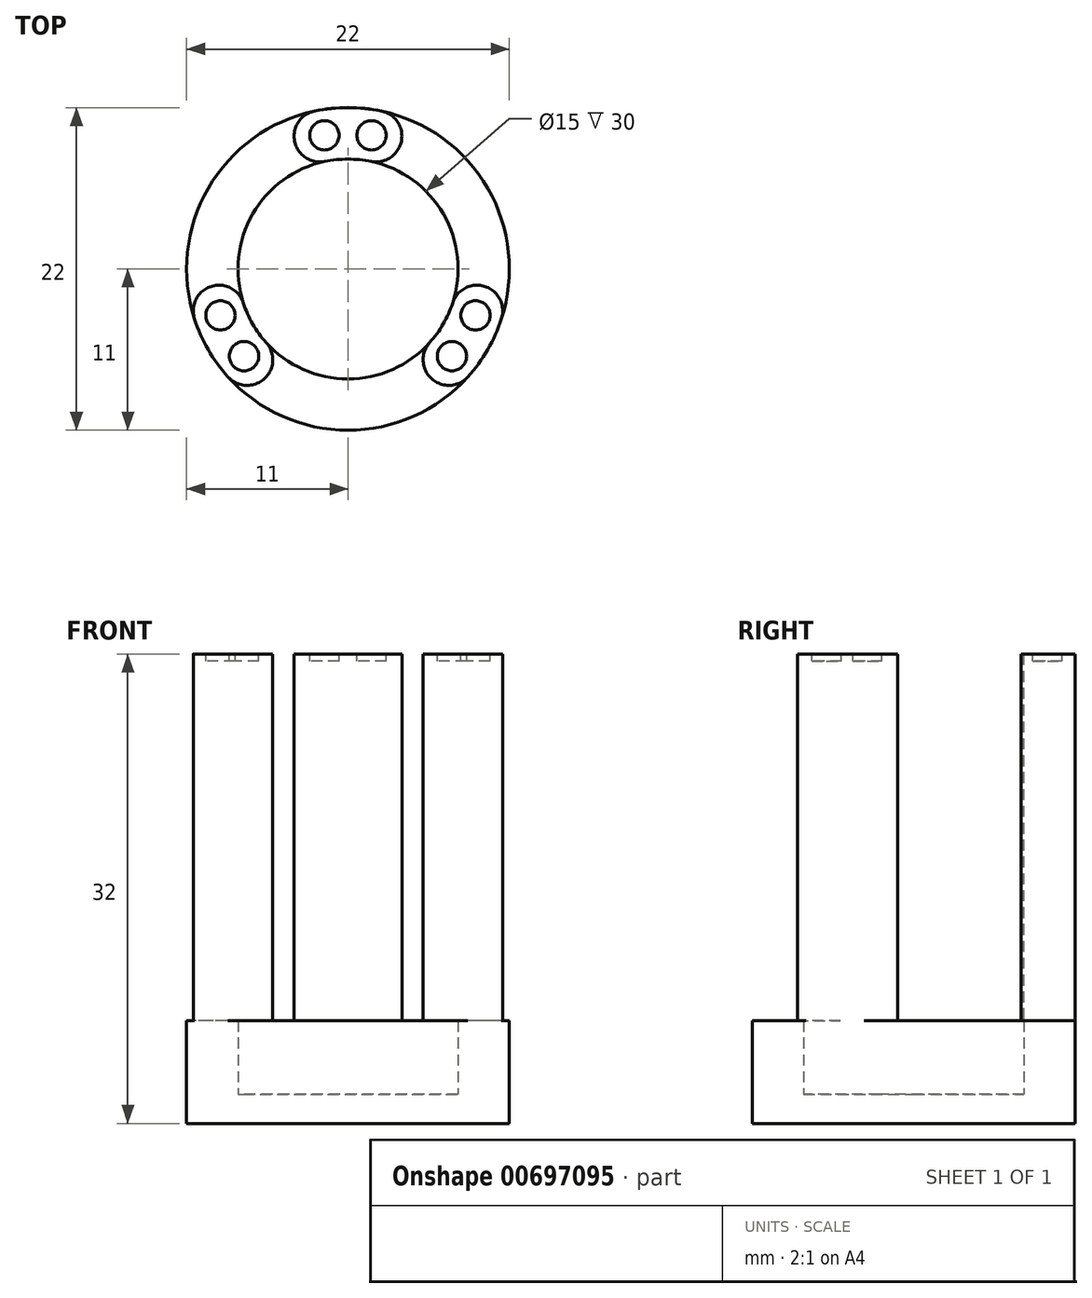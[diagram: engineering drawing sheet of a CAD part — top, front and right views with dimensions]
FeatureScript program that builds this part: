
annotation { "Feature Type Name" : "Feature", "Feature Type Description" : "" }
export const myFeature = defineFeature(function(context is Context, id is Id, definition is map)
    precondition{}
    {
        {
            var Q0;
            Q0=qCreatedBy(makeId("Top.planeOp"),FACE);
            var sketch = newSketch(context, id + "F0", { "sketchPlane" : qUnion([Q0])});
            skCircle(sketch, "E0", {"center": v(0, 0) * mm, "radius": 11 * mm});
            skSolve(sketch);
        }
        {
            var Q0;
            Q0=makeQuery(id+"F0.imprint","IMPRINT",FACE,{"disambiguationData":[TD([[makeQuery(id+"F0.imprint","IMPRINT",EDGE,{"derivedFrom":sQuery(id+"F0.wireOp",EDGE,"E0")}),1.0]])]});
            extrude(context, id + "F1", {"entities" : qUnion([Q0]), "depth" : 2 * mm, "offsetDistance" : 25 * mm});
        }
        {
            var Q0;
            Q0=makeQuery(id+"F1.opExtrude","CAP_FACE",FACE,{"disambiguationData":[OSD([sQuery(id+"F0.wireOp",EDGE,"E0")])],"isStart":false});
            var sketch = newSketch(context, id + "F2", { "sketchPlane" : qUnion([Q0])});
            skCircle(sketch, "E1", {"center": v(0, 0) * mm, "radius": 11 * mm});
            skCircle(sketch, "E2", {"center": v(0, 0) * mm, "radius": 7.5 * mm});
            skSolve(sketch);
        }
        {
            var Q0;
            Q0=makeQuery(id+"F2.imprint","IMPRINT",FACE,{"disambiguationData":[TD([[makeQuery(id+"F2.imprint","IMPRINT",EDGE,{"derivedFrom":sQuery(id+"F2.wireOp",EDGE,"E1")}),1.0]])]});
            extrude(context, id + "F3", {"entities" : qUnion([Q0]), "operationType" : NewBodyOperationType.ADD, "depth" : 5 * mm, "offsetDistance" : 25 * mm});
        }
        {
            var Q0;
            Q0=makeQuery(id+"F3.opExtrude","CAP_FACE",FACE,{"disambiguationData":[OSD([sQuery(id+"F2.wireOp",EDGE,"E1"),sQuery(id+"F2.wireOp",EDGE,"E2")])],"isStart":false});
            var sketch = newSketch(context, id + "F4", { "sketchPlane" : qUnion([Q0])});
            skCircle(sketch, "E3", {"center": v(0, 0) * mm, "radius": 9.25 * mm, "construction": true});
            skLineSegment(sketch, "E4", {"start": v(0, 0) * mm, "end": v(0, 9.25) * mm, "construction": true});
            skLineSegment(sketch, "E5", {"start": v(0, 0) * mm, "end": v(8.01, -4.62) * mm, "construction": true});
            skLineSegment(sketch, "E6", {"start": v(0, 0) * mm, "end": v(-8.01, -4.62) * mm, "construction": true});
            skLineSegment(sketch, "E7", {"start": v(0, 0) * mm, "end": v(1.92, 9.05) * mm, "construction": true});
            skLineSegment(sketch, "E8", {"start": v(0, 0) * mm, "end": v(-1.92, 9.05) * mm, "construction": true});
            skLineSegment(sketch, "E9", {"start": v(0, 0) * mm, "end": v(8.8, -2.86) * mm, "construction": true});
            skLineSegment(sketch, "E10", {"start": v(0, 0) * mm, "end": v(6.87, -6.19) * mm, "construction": true});
            skLineSegment(sketch, "E11", {"start": v(0, 0) * mm, "end": v(-6.87, -6.19) * mm, "construction": true});
            skLineSegment(sketch, "E12", {"start": v(0, 0) * mm, "end": v(-8.8, -2.86) * mm, "construction": true});
            skArc(sketch, "E13", {"start": v(1.92, 9.05) * mm, "mid": v(0, 9.23) * mm, "end": v(-1.92, 9.05) * mm});
            skArc(sketch, "E14", {"start": v(-8.8, -2.86) * mm, "mid": v(-8.01, -4.62) * mm, "end": v(-6.87, -6.19) * mm});
            skArc(sketch, "E15", {"start": v(6.87, -6.19) * mm, "mid": v(8.01, -4.62) * mm, "end": v(8.8, -2.86) * mm});
            skArc(sketch, "E16.0.startCap", {"start": v(2.26, 10.77) * mm, "mid": v(3.64, 8.71) * mm, "end": v(1.59, 7.33) * mm});
            skArc(sketch, "E16.0.endCap", {"start": v(-1.59, 7.33) * mm, "mid": v(-3.64, 8.71) * mm, "end": v(-2.26, 10.77) * mm});
            skArc(sketch, "E16.0.left", {"start": v(1.59, 7.33) * mm, "mid": v(0, 7.48) * mm, "end": v(-1.59, 7.33) * mm});
            skArc(sketch, "E16.0.right", {"start": v(2.26, 10.77) * mm, "mid": v(0, 10.98) * mm, "end": v(-2.26, 10.77) * mm});
            skArc(sketch, "E17.0.startCap", {"start": v(8.17, -7.36) * mm, "mid": v(5.7, -7.49) * mm, "end": v(5.57, -5.02) * mm});
            skArc(sketch, "E17.0.endCap", {"start": v(7.13, -2.32) * mm, "mid": v(9.34, -1.2) * mm, "end": v(10.46, -3.4) * mm});
            skArc(sketch, "E17.0.left", {"start": v(5.57, -5.02) * mm, "mid": v(6.5, -3.75) * mm, "end": v(7.13, -2.32) * mm});
            skArc(sketch, "E17.0.right", {"start": v(8.17, -7.36) * mm, "mid": v(9.53, -5.5) * mm, "end": v(10.46, -3.4) * mm});
            skArc(sketch, "E17.1.startCap", {"start": v(-10.46, -3.4) * mm, "mid": v(-9.34, -1.2) * mm, "end": v(-7.13, -2.32) * mm});
            skArc(sketch, "E17.1.endCap", {"start": v(-5.57, -5.02) * mm, "mid": v(-5.7, -7.49) * mm, "end": v(-8.17, -7.36) * mm});
            skArc(sketch, "E17.1.left", {"start": v(-7.13, -2.32) * mm, "mid": v(-6.5, -3.75) * mm, "end": v(-5.57, -5.02) * mm});
            skArc(sketch, "E17.1.right", {"start": v(-10.46, -3.4) * mm, "mid": v(-9.53, -5.5) * mm, "end": v(-8.17, -7.36) * mm});
            skSolve(sketch);
        }
        {
            var Q0;
            Q0 = qSketchRegion(id + "F4", true);
            extrude(context, id + "F5", {"entities" : qUnion([Q0]), "operationType" : NewBodyOperationType.ADD, "depth" : 25 * mm, "offsetDistance" : 25 * mm});
        }
        {
            var Q0;
            Q0=makeQuery(id+"F5.opExtrude","CAP_FACE",FACE,{"disambiguationData":[OSD([sQuery(id+"F4.wireOp",EDGE,"E16.0.startCap"),sQuery(id+"F4.wireOp",EDGE,"E16.0.endCap"),sQuery(id+"F4.wireOp",EDGE,"E16.0.left"),sQuery(id+"F4.wireOp",EDGE,"E16.0.right")])],"isStart":false});
            var sketch = newSketch(context, id + "F6", { "sketchPlane" : qUnion([Q0])});
            skCircle(sketch, "E18", {"center": v(0, 0) * mm, "radius": 9.25 * mm, "construction": true});
            skLineSegment(sketch, "E19", {"start": v(0, 0) * mm, "end": v(0, 9.25) * mm, "construction": true});
            skLineSegment(sketch, "E20", {"start": v(0, 0) * mm, "end": v(8.01, -4.62) * mm, "construction": true});
            skLineSegment(sketch, "E21", {"start": v(0, 0) * mm, "end": v(-8.01, -4.63) * mm, "construction": true});
            skCircle(sketch, "E22", {"center": v(-1.6, 9.1) * mm, "radius": 1 * mm});
            skCircle(sketch, "E23", {"center": v(-7.09, -5.95) * mm, "radius": 1 * mm});
            skLineSegment(sketch, "E24", {"start": v(0, 0) * mm, "end": v(-1.6, 9.1) * mm, "construction": true});
            skLineSegment(sketch, "E25", {"start": v(0, 0) * mm, "end": v(1.6, 9.1) * mm, "construction": true});
            skCircle(sketch, "E26", {"center": v(1.6, 9.1) * mm, "radius": 1 * mm});
            skLineSegment(sketch, "E27", {"start": v(0, 0) * mm, "end": v(-8.7, -3.16) * mm, "construction": true});
            skLineSegment(sketch, "E28", {"start": v(0, 0) * mm, "end": v(-7.09, -5.95) * mm, "construction": true});
            skCircle(sketch, "E29", {"center": v(-8.7, -3.16) * mm, "radius": 1 * mm});
            skLineSegment(sketch, "E30", {"start": v(0, 0) * mm, "end": v(8.7, -3.16) * mm, "construction": true});
            skLineSegment(sketch, "E31", {"start": v(0, 0) * mm, "end": v(7.09, -5.95) * mm, "construction": true});
            skCircle(sketch, "E32", {"center": v(8.7, -3.16) * mm, "radius": 1 * mm});
            skCircle(sketch, "E33", {"center": v(7.09, -5.95) * mm, "radius": 1 * mm});
            skSolve(sketch);
        }
        {
            var Q0;
            Q0 = qSketchRegion(id + "F6", true);
            extrude(context, id + "F7", {"entities" : qUnion([Q0]), "operationType" : NewBodyOperationType.REMOVE, "oppositeDirection" : true, "depth" : 0.5 * mm, "offsetDistance" : 25 * mm});
        }
    });
